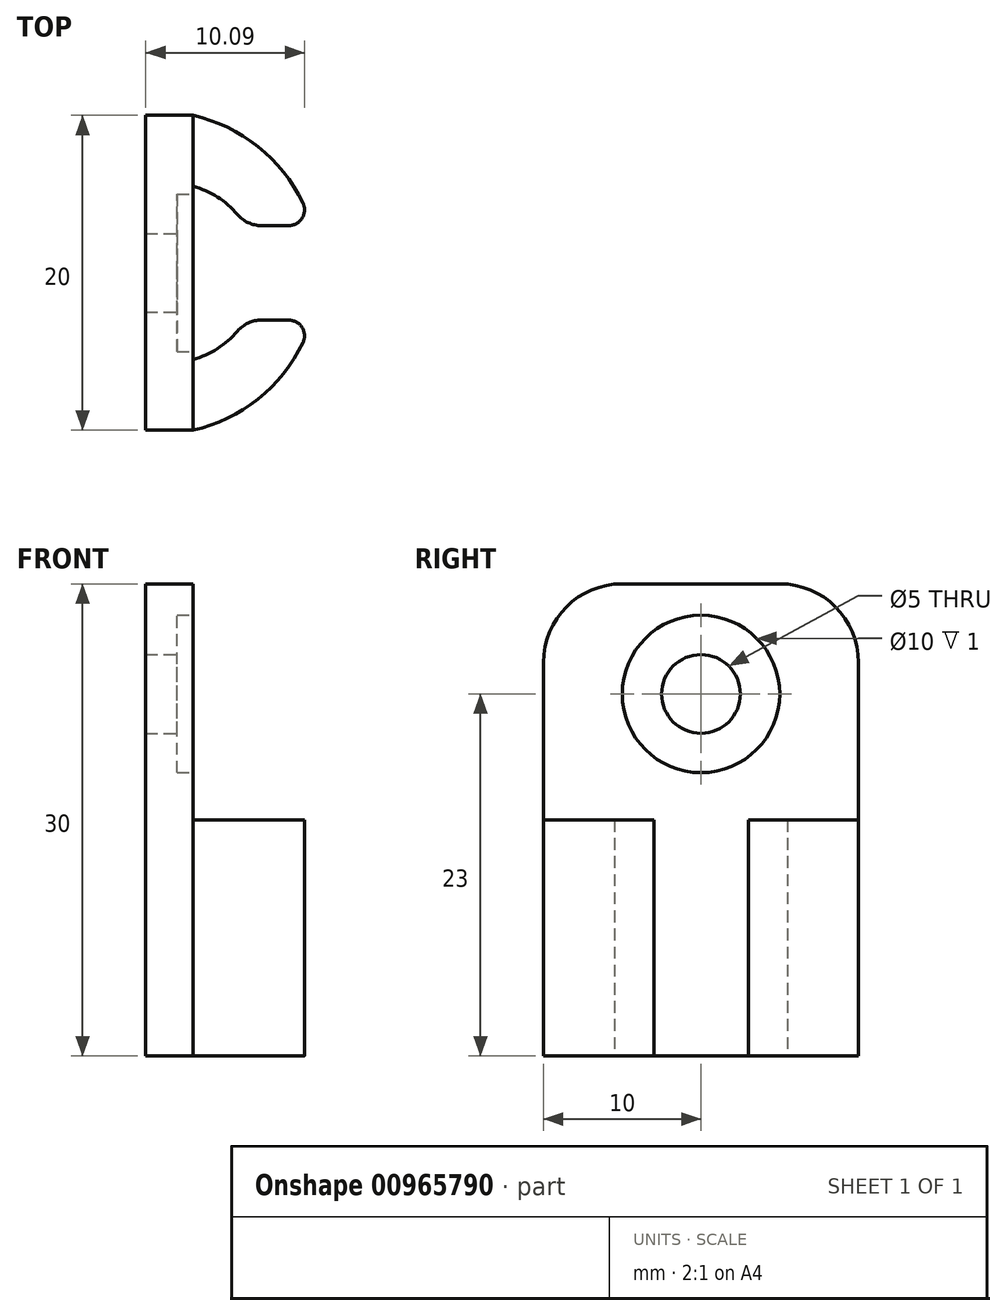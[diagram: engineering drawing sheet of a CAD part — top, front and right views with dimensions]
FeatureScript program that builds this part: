
annotation { "Feature Type Name" : "Feature", "Feature Type Description" : "" }
export const myFeature = defineFeature(function(context is Context, id is Id, definition is map)
    precondition{}
    {
        {
            var Q0;
            Q0=qCreatedBy(makeId("Top.planeOp"),FACE);
            var sketch = newSketch(context, id + "F0", { "sketchPlane" : qUnion([Q0])});
            skLineSegment(sketch, "E0.bottom", {"start": v(0, 10) * mm, "end": v(3, 10) * mm});
            skLineSegment(sketch, "E0.top", {"start": v(0, -10) * mm, "end": v(3, -10) * mm});
            skLineSegment(sketch, "E0.left", {"start": v(0, 10) * mm, "end": v(0, -10) * mm});
            skLineSegment(sketch, "E0.right", {"start": v(3, 10) * mm, "end": v(3, -10) * mm});
            skLineSegment(sketch, "E1.bottom", {"start": v(3, 5.5) * mm, "end": v(5, 5.5) * mm});
            skLineSegment(sketch, "E1.top", {"start": v(3, -5.5) * mm, "end": v(5, -5.5) * mm});
            skLineSegment(sketch, "E1.left", {"start": v(3, 5.5) * mm, "end": v(3, -5.5) * mm});
            skLineSegment(sketch, "E1.right", {"start": v(5, 5.5) * mm, "end": v(5, -5.5) * mm});
            skArc(sketch, "E2", {"start": v(3, -10) * mm, "mid": v(11, 0) * mm, "end": v(3, 10) * mm});
            skLineSegment(sketch, "E3.bottom", {"start": v(5, 3) * mm, "end": v(20, 3) * mm});
            skLineSegment(sketch, "E3.top", {"start": v(5, -3) * mm, "end": v(20, -3) * mm});
            skLineSegment(sketch, "E3.left", {"start": v(5, 3) * mm, "end": v(5, -3) * mm});
            skLineSegment(sketch, "E3.right", {"start": v(20, 3) * mm, "end": v(20, -3) * mm});
            skArc(sketch, "E4", {"start": v(3, -5.5) * mm, "mid": v(7.2, 0) * mm, "end": v(3, 5.5) * mm});
            skSolve(sketch);
        }
        {
            var Q0;
            {var subQ2=sQuery(id+"F0.wireOp",EDGE,"E0.bottom");Q0=makeQuery(id+"F0.imprint","IMPRINT",FACE,{"disambiguationData":[TD([[makeQuery(id+"F0.imprint","IMPRINT",EDGE,{"derivedFrom":subQ2}),-1.0]])]});}
            extrude(context, id + "F1", {"entities" : qUnion([Q0]), "depth" : 30 * mm, "offsetDistance" : 25 * mm});
        }
        {
            var Q0;
            {var subQ5=sQuery(id+"F0.wireOp",EDGE,"E1.bottom");Q0=makeQuery(id+"F0.imprint","IMPRINT",FACE,{"disambiguationData":[TD([[makeQuery(id+"F0.imprint","IMPRINT",EDGE,{"derivedFrom":subQ5}),1.0]])]});}
            var Q1;
            {var subQ5=sQuery(id+"F0.wireOp",EDGE,"E1.top");Q1=makeQuery(id+"F0.imprint","IMPRINT",FACE,{"disambiguationData":[TD([[makeQuery(id+"F0.imprint","IMPRINT",EDGE,{"derivedFrom":subQ5}),-1.0]])]});}
            var Q2;
            {var subQ0=sQuery(id+"F0.wireOp",EDGE,"E1.bottom");Q2=makeQuery(id+"F0.imprint","IMPRINT",FACE,{"disambiguationData":[TD([[makeQuery(id+"F0.imprint","IMPRINT",EDGE,{"derivedFrom":subQ0}),-1.0]])]});}
            var Q3;
            {var subQ0=sQuery(id+"F0.wireOp",EDGE,"E1.top");Q3=makeQuery(id+"F0.imprint","IMPRINT",FACE,{"disambiguationData":[TD([[makeQuery(id+"F0.imprint","IMPRINT",EDGE,{"derivedFrom":subQ0}),1.0]])]});}
            extrude(context, id + "F2", {"entities" : qUnion([Q0, Q1, Q2, Q3]), "operationType" : NewBodyOperationType.ADD, "depth" : 15 * mm, "offsetDistance" : 25 * mm});
        }
        {
            var Q0;
            Q0=makeQuery(id+"F1.opExtrude","SWEPT_FACE",FACE,{"disambiguationData":[OSD([sQuery(id+"F0.wireOp",EDGE,"E0.right"),sQuery(id+"F0.wireOp",EDGE,"E1.left")])]});
            var sketch = newSketch(context, id + "F3", { "sketchPlane" : qUnion([Q0])});
            skCircle(sketch, "E5", {"center": v(0, 23) * mm, "radius": 2.5 * mm});
            skCircle(sketch, "E6", {"center": v(0, 23) * mm, "radius": 5 * mm});
            skSolve(sketch);
        }
        {
            var Q0;
            Q0=makeQuery(id+"F3.imprint","IMPRINT",FACE,{"disambiguationData":[TD([[makeQuery(id+"F3.imprint","IMPRINT",EDGE,{"derivedFrom":sQuery(id+"F3.wireOp",EDGE,"E5")}),1.0]])]});
            extrude(context, id + "F4", {"entities" : qUnion([Q0]), "operationType" : NewBodyOperationType.REMOVE, "oppositeDirection" : true, "depth" : 25 * mm, "offsetDistance" : 25 * mm});
        }
        {
            var Q0;
            Q0=makeQuery(id+"F1.opExtrude","CAP_EDGE",EDGE,{"disambiguationData":[OSD([sQuery(id+"F0.wireOp",EDGE,"E0.top")])],"isStart":false});
            var Q1;
            Q1=makeQuery(id+"F1.opExtrude","CAP_EDGE",EDGE,{"disambiguationData":[OSD([sQuery(id+"F0.wireOp",EDGE,"E0.bottom")])],"isStart":false});
            fillet(context, id + "F5", {"entities" : qUnion([Q0, Q1]), "radius" : 5 * mm, "tangentPropagation" : true, "allowEdgeOverflow" : false});
        }
        {
            var Q0;
            Q0=makeQuery(id+"F3.imprint","IMPRINT",FACE,{"disambiguationData":[TD([[makeQuery(id+"F3.imprint","IMPRINT",EDGE,{"derivedFrom":sQuery(id+"F3.wireOp",EDGE,"E5")}),-1.0]])]});
            extrude(context, id + "F6", {"entities" : qUnion([Q0]), "operationType" : NewBodyOperationType.REMOVE, "oppositeDirection" : true, "depth" : 1 * mm, "offsetDistance" : 25 * mm});
        }
        {
            var Q0;
            Q0=makeQuery(id+"F2.opExtrude","SWEPT_EDGE",EDGE,{"disambiguationData":[OSD([sQuery(id+"F0.wireOp",EDGE,"E3.top"),sQuery(id+"F0.wireOp",EDGE,"E4")])]});
            var Q1;
            Q1=makeQuery(id+"F2.opExtrude","SWEPT_EDGE",EDGE,{"disambiguationData":[OSD([sQuery(id+"F0.wireOp",EDGE,"E3.bottom"),sQuery(id+"F0.wireOp",EDGE,"E4")])]});
            fillet(context, id + "F7", {"entities" : qUnion([Q0, Q1]), "radius" : 2 * mm, "tangentPropagation" : true, "allowEdgeOverflow" : false});
        }
        {
            var Q0;
            Q0=makeQuery(id+"F2.opExtrude","SWEPT_EDGE",EDGE,{"disambiguationData":[OSD([sQuery(id+"F0.wireOp",EDGE,"E2"),sQuery(id+"F0.wireOp",EDGE,"E3.top")])]});
            var Q1;
            Q1=makeQuery(id+"F2.opExtrude","SWEPT_EDGE",EDGE,{"disambiguationData":[OSD([sQuery(id+"F0.wireOp",EDGE,"E2"),sQuery(id+"F0.wireOp",EDGE,"E3.bottom")])]});
            fillet(context, id + "F8", {"entities" : qUnion([Q0, Q1]), "radius" : 1 * mm, "tangentPropagation" : true, "allowEdgeOverflow" : false});
        }
    });
